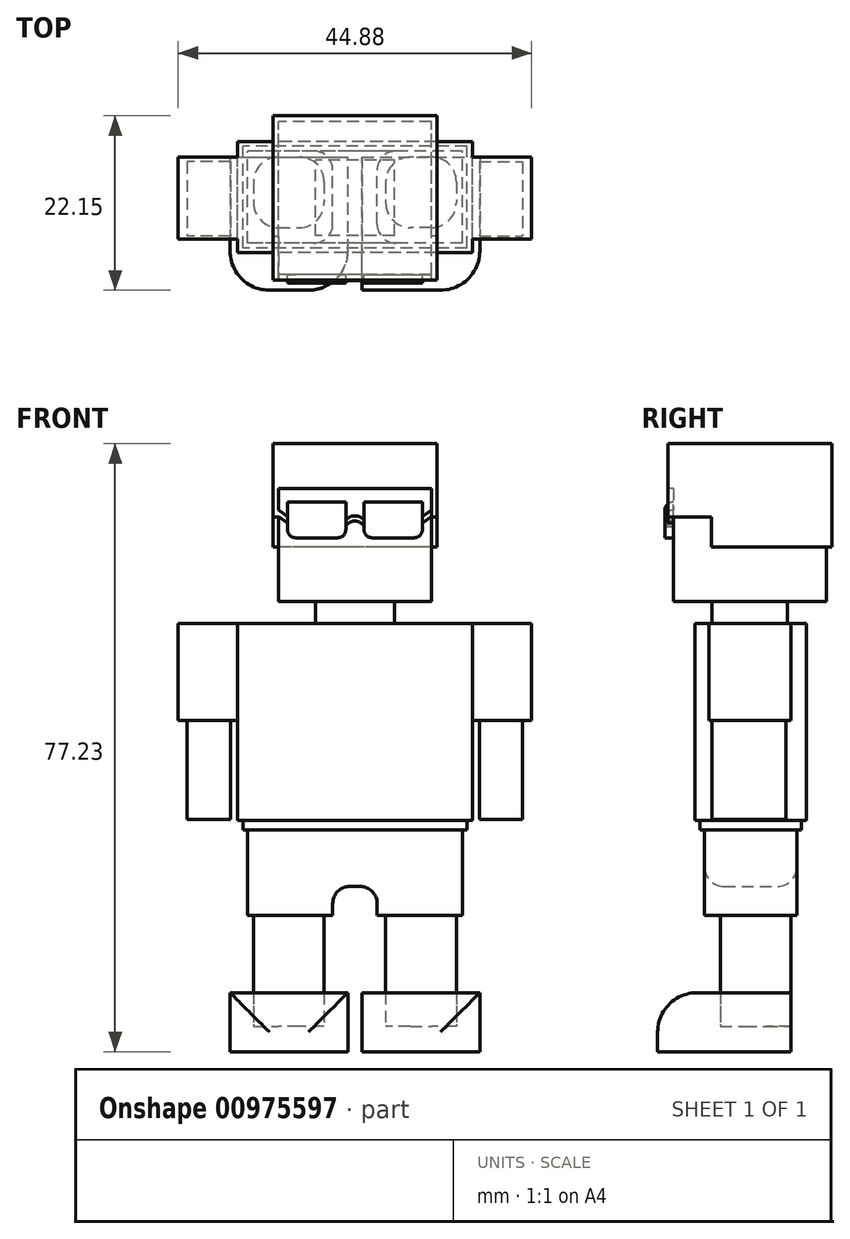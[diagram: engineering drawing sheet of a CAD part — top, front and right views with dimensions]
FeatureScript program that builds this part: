
annotation { "Feature Type Name" : "Feature", "Feature Type Description" : "" }
export const myFeature = defineFeature(function(context is Context, id is Id, definition is map)
    precondition{}
    {
        {
            var Q0;
            Q0=qCreatedBy(makeId("Top.planeOp"),FACE);
            var sketch = newSketch(context, id + "F0", { "sketchPlane" : qUnion([Q0])});
            skLineSegment(sketch, "E0.left", {"start": v(-15.87, 0) * mm, "end": v(-15.87, -16.94) * mm});
            skLineSegment(sketch, "E0.right", {"start": v(15.87, 0) * mm, "end": v(15.87, -16.94) * mm});
            skLineSegment(sketch, "E1", {"start": v(-15.87, 0) * mm, "end": v(15.87, 0) * mm});
            skLineSegment(sketch, "E2", {"start": v(-15.87, -16.94) * mm, "end": v(15.87, -16.94) * mm});
            skLineSegment(sketch, "E3.bottom", {"start": v(0.9, -16.94) * mm, "end": v(-0.9, -16.94) * mm});
            skLineSegment(sketch, "E3.top", {"start": v(0.9, 0) * mm, "end": v(-0.9, 0) * mm});
            skLineSegment(sketch, "E3.left", {"start": v(0.9, -16.94) * mm, "end": v(0.9, 0) * mm});
            skLineSegment(sketch, "E3.right", {"start": v(-0.9, -16.94) * mm, "end": v(-0.9, 0) * mm});
            skPoint(sketch, "E3.middle", {"position": v(0, -8.47) * mm});
            skPoint(sketch, "E3.middle.positionSnap0", {"position": v(15.87, -8.47) * mm});
            skPoint(sketch, "E3.centerSnap0", {"position": v(15.87, -8.47) * mm});
            skSolve(sketch);
        }
        {
            var Q0;
            {var subQ0=sQuery(id+"F0.wireOp",EDGE,"E0.left");Q0=makeQuery(id+"F0.imprint","IMPRINT",FACE,{"disambiguationData":[TD([[makeQuery(id+"F0.imprint","IMPRINT",EDGE,{"derivedFrom":subQ0}),1.0]])]});}
            var Q1;
            {var subQ0=sQuery(id+"F0.wireOp",EDGE,"E3.left");Q1=makeQuery(id+"F0.imprint","IMPRINT",FACE,{"disambiguationData":[TD([[makeQuery(id+"F0.imprint","IMPRINT",EDGE,{"derivedFrom":subQ0}),1.0]])]});}
            var Q2;
            {var subQ0=sQuery(id+"F0.wireOp",EDGE,"E0.right");Q2=makeQuery(id+"F0.imprint","IMPRINT",FACE,{"disambiguationData":[TD([[makeQuery(id+"F0.imprint","IMPRINT",EDGE,{"derivedFrom":subQ0}),-1.0]])]});}
            extrude(context, id + "F1", {"entities" : qUnion([Q0, Q1, Q2]), "depth" : 7.5 * mm, "offsetDistance" : 25 * mm});
        }
        {
            var Q0;
            {var subQ0=sQuery(id+"F0.wireOp",EDGE,"E3.left");Q0=makeQuery(id+"F0.imprint","IMPRINT",FACE,{"disambiguationData":[TD([[makeQuery(id+"F0.imprint","IMPRINT",EDGE,{"derivedFrom":subQ0}),1.0]])]});}
            extrude(context, id + "F2", {"entities" : qUnion([Q0]), "operationType" : NewBodyOperationType.REMOVE, "depth" : 14.2 * mm, "offsetDistance" : 25 * mm});
        }
        {
            var Q0;
            Q0=makeQuery(id+"F1.opExtrude","SWEPT_EDGE",EDGE,{"disambiguationData":[OSD([sQuery(id+"F0.wireOp",EDGE,"E0.left"),sQuery(id+"F0.wireOp",EDGE,"E2")])]});
            var Q1;
            Q1=makeQuery(id+"F2.boolean.opBoolean","COPY",EDGE,{"derivedFrom":makeQuery(id+"F2.opExtrude","SWEPT_EDGE",EDGE,{"disambiguationData":[OSD([sQuery(id+"F0.wireOp",EDGE,"E2"),sQuery(id+"F0.wireOp",EDGE,"E3.right")])]})});
            var Q2;
            Q2=makeQuery(id+"F2.boolean.opBoolean","COPY",EDGE,{"derivedFrom":makeQuery(id+"F2.opExtrude","SWEPT_EDGE",EDGE,{"disambiguationData":[OSD([sQuery(id+"F0.wireOp",EDGE,"E2"),sQuery(id+"F0.wireOp",EDGE,"E3.left")])]})});
            var Q3;
            Q3=makeQuery(id+"F1.opExtrude","SWEPT_EDGE",EDGE,{"disambiguationData":[OSD([sQuery(id+"F0.wireOp",EDGE,"E0.right"),sQuery(id+"F0.wireOp",EDGE,"E2")])]});
            var Q4;
            {var subQ0=sQuery(id+"F0.wireOp",EDGE,"E0.left");var subQ1=sQuery(id+"F0.wireOp",EDGE,"E2");Q4=makeQuery(id+"F2.boolean.opBoolean","SPLIT",EDGE,{"disambiguationData":[TD([makeQuery(id+"F1.opExtrude","SWEPT_FACE",FACE,{"disambiguationData":[OSD([subQ0])]})])],"derivedFrom":makeQuery(id+"F1.opExtrude","CAP_EDGE",EDGE,{"disambiguationData":[OSD([subQ1])],"isStart":false})});}
            var Q5;
            {var subQ0=sQuery(id+"F0.wireOp",EDGE,"E2");var subQ1=sQuery(id+"F0.wireOp",EDGE,"E0.right");Q5=makeQuery(id+"F2.boolean.opBoolean","SPLIT",EDGE,{"disambiguationData":[TD([makeQuery(id+"F1.opExtrude","SWEPT_FACE",FACE,{"disambiguationData":[OSD([subQ1])]})])],"derivedFrom":makeQuery(id+"F1.opExtrude","CAP_EDGE",EDGE,{"disambiguationData":[OSD([subQ0])],"isStart":false})});}
            fillet(context, id + "F3", {"entities" : qUnion([Q0, Q1, Q2, Q3, Q4, Q5]), "tangentPropagation" : true, "radius" : 5 * mm, "defaultsChanged" : false, "vertexSettings" : [], "allowEdgeOverflow" : false});
        }
        {
            var Q0;
            {var subQ0=sQuery(id+"F0.wireOp",EDGE,"E0.left");var subQ1=sQuery(id+"F0.wireOp",EDGE,"E2");var subQ2=sQuery(id+"F0.wireOp",EDGE,"E1");Q0=makeQuery(id+"F2.boolean.opBoolean","SPLIT",FACE,{"disambiguationData":[TD([makeQuery(id+"F1.opExtrude","SWEPT_FACE",FACE,{"disambiguationData":[OSD([subQ0])]})])],"derivedFrom":makeQuery(id+"F1.opExtrude","CAP_FACE",FACE,{"disambiguationData":[OSD([subQ0,sQuery(id+"F0.wireOp",EDGE,"E0.right"),subQ2,subQ1])],"isStart":false})});}
            var sketch = newSketch(context, id + "F4", { "sketchPlane" : qUnion([Q0])});
            skLineSegment(sketch, "E4.bottom", {"start": v(-3.9, -8.98) * mm, "end": v(-12.87, -8.98) * mm});
            skLineSegment(sketch, "E4.top", {"start": v(-3.9, -0.01) * mm, "end": v(-12.87, -0.01) * mm});
            skLineSegment(sketch, "E4.left", {"start": v(-3.9, -8.98) * mm, "end": v(-3.9, -0.01) * mm});
            skLineSegment(sketch, "E4.right", {"start": v(-12.87, -8.98) * mm, "end": v(-12.87, -0.01) * mm});
            skPoint(sketch, "E4.middle", {"position": v(-8.39, -4.5) * mm});
            skPoint(sketch, "E4.middle.positionSnap0", {"position": v(-8.39, 0) * mm});
            skPoint(sketch, "E4.centerSnap0", {"position": v(-8.39, 0) * mm});
            skLineSegment(sketch, "E5.MirrorCS", {"start": v(3.9, -8.98) * mm, "end": v(3.9, -0.01) * mm});
            skLineSegment(sketch, "E6.MirrorCS", {"start": v(3.9, -8.98) * mm, "end": v(12.87, -8.98) * mm});
            skLineSegment(sketch, "E7.MirrorCS", {"start": v(12.87, -8.98) * mm, "end": v(12.87, -0.01) * mm});
            skLineSegment(sketch, "E8.MirrorCS", {"start": v(3.9, -0.01) * mm, "end": v(12.87, -0.01) * mm});
            skSolve(sketch);
        }
        {
            var Q0;
            Q0=makeQuery(id+"F4.imprint","IMPRINT",FACE,{"disambiguationData":[TD([[makeQuery(id+"F4.imprint","IMPRINT",EDGE,{"derivedFrom":sQuery(id+"F4.wireOp",EDGE,"E4.bottom")}),-1.0]])]});
            var Q1;
            Q1=makeQuery(id+"F4.imprint","IMPRINT",FACE,{"disambiguationData":[TD([[makeQuery(id+"F4.imprint","IMPRINT",EDGE,{"derivedFrom":sQuery(id+"F4.wireOp",EDGE,"E5.MirrorCS")}),-1.0]])]});
            extrude(context, id + "F5", {"entities" : qUnion([Q0, Q1]), "depth" : 13.5 * mm, "offsetDistance" : 25 * mm, "hasSecondDirection" : true, "secondDirectionOppositeDirection" : true, "secondDirectionDepth" : 4.3 * mm});
        }
        {
            var Q0;
            Q0=makeQuery(id+"F5.opExtrude","SWEPT_EDGE",EDGE,{"disambiguationData":[OSD([sQuery(id+"F4.wireOp",EDGE,"E4.bottom"),sQuery(id+"F4.wireOp",EDGE,"E4.right")])]});
            var Q1;
            Q1=makeQuery(id+"F5.opExtrude","SWEPT_EDGE",EDGE,{"disambiguationData":[OSD([sQuery(id+"F4.wireOp",EDGE,"E4.bottom"),sQuery(id+"F4.wireOp",EDGE,"E4.left")])]});
            var Q2;
            Q2=makeQuery(id+"F5.opExtrude","SWEPT_EDGE",EDGE,{"disambiguationData":[OSD([sQuery(id+"F4.wireOp",EDGE,"E5.MirrorCS"),sQuery(id+"F4.wireOp",EDGE,"E6.MirrorCS")])]});
            var Q3;
            Q3=makeQuery(id+"F5.opExtrude","SWEPT_EDGE",EDGE,{"disambiguationData":[OSD([sQuery(id+"F4.wireOp",EDGE,"E4.top"),sQuery(id+"F4.wireOp",EDGE,"E4.right")])]});
            var Q4;
            Q4=makeQuery(id+"F5.opExtrude","SWEPT_EDGE",EDGE,{"disambiguationData":[OSD([sQuery(id+"F4.wireOp",EDGE,"E4.top"),sQuery(id+"F4.wireOp",EDGE,"E4.left")])]});
            var Q5;
            Q5=makeQuery(id+"F5.opExtrude","SWEPT_EDGE",EDGE,{"disambiguationData":[OSD([sQuery(id+"F4.wireOp",EDGE,"E6.MirrorCS"),sQuery(id+"F4.wireOp",EDGE,"E7.MirrorCS")])]});
            var Q6;
            Q6=makeQuery(id+"F5.opExtrude","SWEPT_EDGE",EDGE,{"disambiguationData":[OSD([sQuery(id+"F4.wireOp",EDGE,"E7.MirrorCS"),sQuery(id+"F4.wireOp",EDGE,"E8.MirrorCS")])]});
            var Q7;
            Q7=makeQuery(id+"F5.opExtrude","SWEPT_EDGE",EDGE,{"disambiguationData":[OSD([sQuery(id+"F4.wireOp",EDGE,"E5.MirrorCS"),sQuery(id+"F4.wireOp",EDGE,"E8.MirrorCS")])]});
            fillet(context, id + "F6", {"entities" : qUnion([Q0, Q1, Q2, Q3, Q4, Q5, Q6, Q7]), "tangentPropagation" : true, "radius" : 3.14 * mm, "defaultsChanged" : false, "vertexSettings" : [], "allowEdgeOverflow" : false});
        }
        {
            var Q0;
            Q0=makeQuery(id+"F5.opExtrude","CAP_FACE",FACE,{"disambiguationData":[OSD([sQuery(id+"F4.wireOp",EDGE,"E4.bottom"),sQuery(id+"F4.wireOp",EDGE,"E4.top"),sQuery(id+"F4.wireOp",EDGE,"E4.left"),sQuery(id+"F4.wireOp",EDGE,"E4.right")])],"isStart":false});
            var sketch = newSketch(context, id + "F7", { "sketchPlane" : qUnion([Q0])});
            skLineSegment(sketch, "E9.bottom", {"start": v(13.64, -10.96) * mm, "end": v(-13.64, -10.96) * mm});
            skLineSegment(sketch, "E9.top", {"start": v(13.64, 0.74) * mm, "end": v(-13.64, 0.74) * mm});
            skLineSegment(sketch, "E9.left", {"start": v(13.64, -10.96) * mm, "end": v(13.64, 0.74) * mm});
            skLineSegment(sketch, "E9.right", {"start": v(-13.64, -10.96) * mm, "end": v(-13.64, 0.74) * mm});
            skPoint(sketch, "E9.middle", {"position": v(0, -5.1) * mm});
            skSolve(sketch);
        }
        {
            var Q0;
            Q0 = qSketchRegion(id + "F7", true);
            extrude(context, id + "F8", {"entities" : qUnion([Q0]), "depth" : 7.2 * mm, "offsetDistance" : 25 * mm});
        }
        {
            var Q0;
            Q0=makeQuery(id+"F8.opExtrude","CAP_FACE",FACE,{"disambiguationData":[OSD([sQuery(id+"F7.wireOp",EDGE,"E9.bottom"),sQuery(id+"F7.wireOp",EDGE,"E9.top"),sQuery(id+"F7.wireOp",EDGE,"E9.left"),sQuery(id+"F7.wireOp",EDGE,"E9.right")])],"isStart":true});
            var sketch = newSketch(context, id + "F9", { "sketchPlane" : qUnion([Q0])});
            skLineSegment(sketch, "E10.bottom", {"start": v(-13.64, 10.96) * mm, "end": v(-2.82, 10.96) * mm});
            skLineSegment(sketch, "E10.top", {"start": v(-13.64, -0.74) * mm, "end": v(-2.82, -0.74) * mm});
            skLineSegment(sketch, "E10.left", {"start": v(-13.64, 10.96) * mm, "end": v(-13.64, -0.74) * mm});
            skLineSegment(sketch, "E10.right", {"start": v(-2.82, 10.96) * mm, "end": v(-2.82, -0.74) * mm});
            skLineSegment(sketch, "E11.MirrorCS", {"start": v(13.64, 10.96) * mm, "end": v(2.82, 10.96) * mm});
            skLineSegment(sketch, "E12.MirrorCS", {"start": v(13.64, 10.96) * mm, "end": v(13.64, -0.74) * mm});
            skLineSegment(sketch, "E13.MirrorCS", {"start": v(13.64, -0.74) * mm, "end": v(2.82, -0.74) * mm});
            skLineSegment(sketch, "E14.MirrorCS", {"start": v(2.82, 10.96) * mm, "end": v(2.82, -0.74) * mm});
            skSolve(sketch);
        }
        {
            var Q0;
            Q0=makeQuery(id+"F9.imprint","IMPRINT",FACE,{"disambiguationData":[TD([[makeQuery(id+"F9.imprint","IMPRINT",EDGE,{"derivedFrom":sQuery(id+"F9.wireOp",EDGE,"E10.bottom")}),1.0]])]});
            var Q1;
            Q1=makeQuery(id+"F9.imprint","IMPRINT",FACE,{"disambiguationData":[TD([[makeQuery(id+"F9.imprint","IMPRINT",EDGE,{"derivedFrom":sQuery(id+"F9.wireOp",EDGE,"E11.MirrorCS")}),1.0]])]});
            extrude(context, id + "F10", {"entities" : qUnion([Q0, Q1]), "operationType" : NewBodyOperationType.ADD, "depth" : 3.7 * mm, "offsetDistance" : 25 * mm, "hasSecondDirection" : true, "secondDirectionOppositeDirection" : true, "secondDirectionDepth" : 2.3 * mm});
        }
        {
            var Q0;
            Q0=makeQuery(id+"F10.boolean.opBoolean","INTERSECT",EDGE,{"derivedFrom":[makeQuery(id+"F8.opExtrude","CAP_FACE",FACE,{"disambiguationData":[OSD([sQuery(id+"F7.wireOp",EDGE,"E9.bottom"),sQuery(id+"F7.wireOp",EDGE,"E9.top"),sQuery(id+"F7.wireOp",EDGE,"E9.left"),sQuery(id+"F7.wireOp",EDGE,"E9.right")])],"isStart":true}),makeQuery(id+"F10.opExtrude","SWEPT_FACE",FACE,{"disambiguationData":[OSD([sQuery(id+"F9.wireOp",EDGE,"E14.MirrorCS")])]})]});
            var Q1;
            Q1=makeQuery(id+"F10.boolean.opBoolean","INTERSECT",EDGE,{"derivedFrom":[makeQuery(id+"F8.opExtrude","CAP_FACE",FACE,{"disambiguationData":[OSD([sQuery(id+"F7.wireOp",EDGE,"E9.bottom"),sQuery(id+"F7.wireOp",EDGE,"E9.top"),sQuery(id+"F7.wireOp",EDGE,"E9.left"),sQuery(id+"F7.wireOp",EDGE,"E9.right")])],"isStart":true}),makeQuery(id+"F10.opExtrude","SWEPT_FACE",FACE,{"disambiguationData":[OSD([sQuery(id+"F9.wireOp",EDGE,"E10.right")])]})]});
            fillet(context, id + "F11", {"entities" : qUnion([Q0, Q1]), "tangentPropagation" : true, "radius" : 2.17 * mm, "defaultsChanged" : false, "vertexSettings" : [], "allowEdgeOverflow" : false});
        }
        {
            var Q0;
            {var subQ0=sQuery(id+"F7.wireOp",EDGE,"E9.top");Q0=makeQuery(id+"F11.opFillet","BLEND_EDGE",EDGE,{"blendedFrom":[makeQuery(id+"F10.boolean.opBoolean","INTERSECT",EDGE,{"derivedFrom":[makeQuery(id+"F8.opExtrude","CAP_FACE",FACE,{"disambiguationData":[OSD([sQuery(id+"F7.wireOp",EDGE,"E9.bottom"),subQ0,sQuery(id+"F7.wireOp",EDGE,"E9.left"),sQuery(id+"F7.wireOp",EDGE,"E9.right")])],"isStart":true}),makeQuery(id+"F10.opExtrude","SWEPT_FACE",FACE,{"disambiguationData":[OSD([sQuery(id+"F9.wireOp",EDGE,"E14.MirrorCS")])]})]}),makeQuery(id+"F10.boolean.opBoolean","MERGE",FACE,{"derivedFrom":[makeQuery(id+"F8.opExtrude","SWEPT_FACE",FACE,{"disambiguationData":[OSD([subQ0])]}),makeQuery(id+"F10.opExtrude","SWEPT_FACE",FACE,{"disambiguationData":[OSD([sQuery(id+"F9.wireOp",EDGE,"E10.top")])]}),makeQuery(id+"F10.opExtrude","SWEPT_FACE",FACE,{"disambiguationData":[OSD([sQuery(id+"F9.wireOp",EDGE,"E13.MirrorCS")])]})]})],"blendedInto":[makeQuery(id+"F10.boolean.opBoolean","MERGE",FACE,{"derivedFrom":[makeQuery(id+"F8.opExtrude","SWEPT_FACE",FACE,{"disambiguationData":[OSD([subQ0])]}),makeQuery(id+"F10.opExtrude","SWEPT_FACE",FACE,{"disambiguationData":[OSD([sQuery(id+"F9.wireOp",EDGE,"E10.top")])]}),makeQuery(id+"F10.opExtrude","SWEPT_FACE",FACE,{"disambiguationData":[OSD([sQuery(id+"F9.wireOp",EDGE,"E13.MirrorCS")])]})]})]});}
            var Q1;
            {var subQ0=sQuery(id+"F7.wireOp",EDGE,"E9.bottom");Q1=makeQuery(id+"F11.opFillet","BLEND_EDGE",EDGE,{"blendedFrom":[makeQuery(id+"F10.boolean.opBoolean","INTERSECT",EDGE,{"derivedFrom":[makeQuery(id+"F8.opExtrude","CAP_FACE",FACE,{"disambiguationData":[OSD([subQ0,sQuery(id+"F7.wireOp",EDGE,"E9.top"),sQuery(id+"F7.wireOp",EDGE,"E9.left"),sQuery(id+"F7.wireOp",EDGE,"E9.right")])],"isStart":true}),makeQuery(id+"F10.opExtrude","SWEPT_FACE",FACE,{"disambiguationData":[OSD([sQuery(id+"F9.wireOp",EDGE,"E10.right")])]})]}),makeQuery(id+"F10.boolean.opBoolean","MERGE",FACE,{"derivedFrom":[makeQuery(id+"F8.opExtrude","SWEPT_FACE",FACE,{"disambiguationData":[OSD([subQ0])]}),makeQuery(id+"F10.opExtrude","SWEPT_FACE",FACE,{"disambiguationData":[OSD([sQuery(id+"F9.wireOp",EDGE,"E10.bottom")])]}),makeQuery(id+"F10.opExtrude","SWEPT_FACE",FACE,{"disambiguationData":[OSD([sQuery(id+"F9.wireOp",EDGE,"E11.MirrorCS")])]})]})],"blendedInto":[makeQuery(id+"F10.boolean.opBoolean","MERGE",FACE,{"derivedFrom":[makeQuery(id+"F8.opExtrude","SWEPT_FACE",FACE,{"disambiguationData":[OSD([subQ0])]}),makeQuery(id+"F10.opExtrude","SWEPT_FACE",FACE,{"disambiguationData":[OSD([sQuery(id+"F9.wireOp",EDGE,"E10.bottom")])]}),makeQuery(id+"F10.opExtrude","SWEPT_FACE",FACE,{"disambiguationData":[OSD([sQuery(id+"F9.wireOp",EDGE,"E11.MirrorCS")])]})]})]});}
            fillet(context, id + "F12", {"entities" : qUnion([Q0, Q1]), "tangentPropagation" : true, "radius" : 2.41 * mm, "defaultsChanged" : false, "vertexSettings" : [], "allowEdgeOverflow" : false});
        }
        {
            var Q0;
            Q0=makeQuery(id+"F8.opExtrude","CAP_FACE",FACE,{"disambiguationData":[OSD([sQuery(id+"F7.wireOp",EDGE,"E9.bottom"),sQuery(id+"F7.wireOp",EDGE,"E9.top"),sQuery(id+"F7.wireOp",EDGE,"E9.left"),sQuery(id+"F7.wireOp",EDGE,"E9.right")])],"isStart":false});
            var sketch = newSketch(context, id + "F13", { "sketchPlane" : qUnion([Q0])});
            skLineSegment(sketch, "E15.bottom", {"start": v(14.22, -11.56) * mm, "end": v(-14.22, -11.56) * mm});
            skLineSegment(sketch, "E15.top", {"start": v(14.22, 1.34) * mm, "end": v(-14.22, 1.34) * mm});
            skLineSegment(sketch, "E15.left", {"start": v(14.22, -11.56) * mm, "end": v(14.22, 1.34) * mm});
            skLineSegment(sketch, "E15.right", {"start": v(-14.22, -11.56) * mm, "end": v(-14.22, 1.34) * mm});
            skPoint(sketch, "E15.middle", {"position": v(0, -5.1) * mm});
            skPoint(sketch, "E15.middle.positionSnap0", {"position": v(13.64, -5.1) * mm});
            skPoint(sketch, "E15.centerSnap0", {"position": v(13.64, -5.1) * mm});
            skSolve(sketch);
        }
        {
            var Q0;
            Q0 = qSketchRegion(id + "F13", true);
            extrude(context, id + "F14", {"entities" : qUnion([Q0]), "operationType" : NewBodyOperationType.ADD, "depth" : 1.2 * mm, "offsetDistance" : 25 * mm});
        }
        {
            var Q0;
            Q0=makeQuery(id+"F14.opExtrude","CAP_FACE",FACE,{"disambiguationData":[OSD([sQuery(id+"F13.wireOp",EDGE,"E15.bottom"),sQuery(id+"F13.wireOp",EDGE,"E15.top"),sQuery(id+"F13.wireOp",EDGE,"E15.left"),sQuery(id+"F13.wireOp",EDGE,"E15.right")])],"isStart":false});
            var sketch = newSketch(context, id + "F15", { "sketchPlane" : qUnion([Q0])});
            skLineSegment(sketch, "E16.bottom", {"start": v(14.94, -12.17) * mm, "end": v(-14.94, -12.17) * mm});
            skLineSegment(sketch, "E16.top", {"start": v(14.94, 1.95) * mm, "end": v(-14.94, 1.95) * mm});
            skLineSegment(sketch, "E16.left", {"start": v(14.94, -12.17) * mm, "end": v(14.94, 1.95) * mm});
            skLineSegment(sketch, "E16.right", {"start": v(-14.94, -12.17) * mm, "end": v(-14.94, 1.95) * mm});
            skPoint(sketch, "E16.middle", {"position": v(0, -5.1) * mm});
            skPoint(sketch, "E16.middle.positionSnap0", {"position": v(14.22, -5.1) * mm});
            skPoint(sketch, "E16.centerSnap0", {"position": v(14.22, -5.1) * mm});
            skSolve(sketch);
        }
        {
            var Q0;
            Q0=makeQuery(id+"F15.imprint","IMPRINT",FACE,{"disambiguationData":[TD([[makeQuery(id+"F15.imprint","IMPRINT",EDGE,{"derivedFrom":sQuery(id+"F15.wireOp",EDGE,"E16.bottom")}),-1.0]])]});
            var Q1;
            Q1=makeQuery(id+"F15.imprint","IMPRINT",FACE,{"disambiguationData":[TD([[makeQuery(id+"F15.imprint","IMPRINT",EDGE,{"derivedFrom":makeQuery(id+"F14.opExtrude","CAP_EDGE",EDGE,{"disambiguationData":[OSD([sQuery(id+"F13.wireOp",EDGE,"E15.bottom")])],"isStart":false})}),-1.0]])]});
            extrude(context, id + "F16", {"entities" : qUnion([Q0, Q1]), "depth" : 25 * mm, "offsetDistance" : 25 * mm});
        }
        {
            var Q0;
            Q0=makeQuery(id+"F16.opExtrude","SWEPT_FACE",FACE,{"disambiguationData":[OSD([sQuery(id+"F15.wireOp",EDGE,"E16.right")])]});
            var sketch = newSketch(context, id + "F17", { "sketchPlane" : qUnion([Q0])});
            skLineSegment(sketch, "E17.bottom", {"start": v(0, 54.4) * mm, "end": v(10.42, 54.4) * mm});
            skLineSegment(sketch, "E17.top", {"start": v(0, 42.1) * mm, "end": v(10.42, 42.1) * mm});
            skLineSegment(sketch, "E17.left", {"start": v(0, 54.4) * mm, "end": v(0, 42.1) * mm});
            skLineSegment(sketch, "E17.right", {"start": v(10.42, 54.4) * mm, "end": v(10.42, 42.1) * mm});
            skSolve(sketch);
        }
        {
            var Q0;
            Q0 = qSketchRegion(id + "F17", true);
            extrude(context, id + "F18", {"entities" : qUnion([Q0]), "operationType" : NewBodyOperationType.ADD, "depth" : 7.5 * mm, "offsetDistance" : 25 * mm, "hasSecondDirection" : true, "secondDirectionOppositeDirection" : true, "secondDirectionDepth" : 37.38 * mm});
        }
        {
            var Q0;
            {var subQ2=sQuery(id+"F17.wireOp",EDGE,"E17.top");Q0=makeQuery(id+"F18.boolean.opBoolean","SPLIT",FACE,{"disambiguationData":[TD([makeQuery(id+"F16.opExtrude","SWEPT_FACE",FACE,{"disambiguationData":[OSD([sQuery(id+"F15.wireOp",EDGE,"E16.right")])]})])],"derivedFrom":makeQuery(id+"F18.opExtrude","SWEPT_FACE",FACE,{"disambiguationData":[OSD([subQ2])]})});}
            var sketch = newSketch(context, id + "F19", { "sketchPlane" : qUnion([Q0])});
            skLineSegment(sketch, "E18.bottom", {"start": v(-15.8, 0.63) * mm, "end": v(-21.3, 0.63) * mm});
            skLineSegment(sketch, "E18.top", {"start": v(-15.8, 10.06) * mm, "end": v(-21.3, 10.06) * mm});
            skLineSegment(sketch, "E18.left", {"start": v(-15.8, 0.63) * mm, "end": v(-15.8, 10.06) * mm});
            skLineSegment(sketch, "E18.right", {"start": v(-21.3, 0.63) * mm, "end": v(-21.3, 10.06) * mm});
            skPoint(sketch, "E18.middle", {"position": v(-19.05, 5.34) * mm});
            skLineSegment(sketch, "E19.MirrorCS", {"start": v(15.8, 0.63) * mm, "end": v(21.3, 0.63) * mm});
            skLineSegment(sketch, "E20.MirrorCS", {"start": v(15.8, 0.63) * mm, "end": v(15.8, 10.06) * mm});
            skLineSegment(sketch, "E21.MirrorCS", {"start": v(15.8, 10.06) * mm, "end": v(21.3, 10.06) * mm});
            skLineSegment(sketch, "E22.MirrorCS", {"start": v(21.3, 0.63) * mm, "end": v(21.3, 10.06) * mm});
            skSolve(sketch);
        }
        {
            var Q0;
            Q0=makeQuery(id+"F19.imprint","IMPRINT",FACE,{"disambiguationData":[TD([[makeQuery(id+"F19.imprint","IMPRINT",EDGE,{"derivedFrom":sQuery(id+"F19.wireOp",EDGE,"E18.bottom")}),-1.0]])]});
            var Q1;
            Q1=makeQuery(id+"F19.imprint","IMPRINT",FACE,{"disambiguationData":[TD([[makeQuery(id+"F19.imprint","IMPRINT",EDGE,{"derivedFrom":sQuery(id+"F19.wireOp",EDGE,"E19.MirrorCS")}),1.0]])]});
            extrude(context, id + "F20", {"entities" : qUnion([Q0, Q1]), "depth" : 12.6 * mm, "offsetDistance" : 25 * mm});
        }
        {
            var Q0;
            Q0=makeQuery(id+"F18.boolean.opBoolean","MERGE",FACE,{"derivedFrom":[makeQuery(id+"F16.opExtrude","CAP_FACE",FACE,{"disambiguationData":[OSD([sQuery(id+"F15.wireOp",EDGE,"E16.bottom"),sQuery(id+"F15.wireOp",EDGE,"E16.top"),sQuery(id+"F15.wireOp",EDGE,"E16.left"),sQuery(id+"F15.wireOp",EDGE,"E16.right")])],"isStart":false}),makeQuery(id+"F18.opExtrude","SWEPT_FACE",FACE,{"disambiguationData":[OSD([sQuery(id+"F17.wireOp",EDGE,"E17.bottom")])]})]});
            var sketch = newSketch(context, id + "F21", { "sketchPlane" : qUnion([Q0])});
            skLineSegment(sketch, "E23.bottom", {"start": v(5.03, -10) * mm, "end": v(-5.03, -10) * mm});
            skLineSegment(sketch, "E23.top", {"start": v(5.03, -0.42) * mm, "end": v(-5.03, -0.42) * mm});
            skLineSegment(sketch, "E23.left", {"start": v(5.03, -10) * mm, "end": v(5.03, -0.42) * mm});
            skLineSegment(sketch, "E23.right", {"start": v(-5.03, -10) * mm, "end": v(-5.03, -0.42) * mm});
            skPoint(sketch, "E23.middle", {"position": v(0, -5.21) * mm});
            skPoint(sketch, "E23.middle.positionSnap0", {"position": v(22.44, -5.21) * mm});
            skPoint(sketch, "E23.centerSnap0", {"position": v(22.44, -5.21) * mm});
            skSolve(sketch);
        }
        {
            var Q0;
            Q0 = qSketchRegion(id + "F21", true);
            extrude(context, id + "F22", {"entities" : qUnion([Q0]), "depth" : 2.8 * mm, "offsetDistance" : 25 * mm});
        }
        {
            var Q0;
            Q0=makeQuery(id+"F22.opExtrude","CAP_FACE",FACE,{"disambiguationData":[OSD([sQuery(id+"F21.wireOp",EDGE,"E23.bottom"),sQuery(id+"F21.wireOp",EDGE,"E23.top"),sQuery(id+"F21.wireOp",EDGE,"E23.left"),sQuery(id+"F21.wireOp",EDGE,"E23.right")])],"isStart":false});
            var sketch = newSketch(context, id + "F23", { "sketchPlane" : qUnion([Q0])});
            skLineSegment(sketch, "E24.bottom", {"start": v(9.72, -14.93) * mm, "end": v(-9.72, -14.93) * mm});
            skLineSegment(sketch, "E24.top", {"start": v(9.72, 4.5) * mm, "end": v(-9.72, 4.5) * mm});
            skLineSegment(sketch, "E24.left", {"start": v(9.72, -14.93) * mm, "end": v(9.72, 4.5) * mm});
            skLineSegment(sketch, "E24.right", {"start": v(-9.72, -14.93) * mm, "end": v(-9.72, 4.5) * mm});
            skPoint(sketch, "E24.middle", {"position": v(0, -5.21) * mm});
            skPoint(sketch, "E24.middle.positionSnap0", {"position": v(5.03, -5.21) * mm});
            skPoint(sketch, "E24.centerSnap0", {"position": v(5.03, -5.21) * mm});
            skSolve(sketch);
        }
        {
            var Q0;
            Q0=makeQuery(id+"F23.imprint","IMPRINT",FACE,{"disambiguationData":[TD([[makeQuery(id+"F23.imprint","IMPRINT",EDGE,{"derivedFrom":sQuery(id+"F23.wireOp",EDGE,"E24.bottom")}),-1.0]])]});
            var Q1;
            Q1=makeQuery(id+"F23.imprint","IMPRINT",FACE,{"disambiguationData":[TD([[makeQuery(id+"F23.imprint","IMPRINT",EDGE,{"derivedFrom":makeQuery(id+"F22.opExtrude","CAP_EDGE",EDGE,{"disambiguationData":[OSD([sQuery(id+"F21.wireOp",EDGE,"E23.bottom")])],"isStart":false})}),-1.0]])]});
            extrude(context, id + "F24", {"entities" : qUnion([Q0, Q1]), "operationType" : NewBodyOperationType.ADD, "depth" : 19.43 * mm, "offsetDistance" : 25 * mm});
        }
        {
            var Q0;
            Q0=makeQuery(id+"F24.opExtrude","CAP_FACE",FACE,{"disambiguationData":[OSD([sQuery(id+"F23.wireOp",EDGE,"E24.bottom"),sQuery(id+"F23.wireOp",EDGE,"E24.top"),sQuery(id+"F23.wireOp",EDGE,"E24.left"),sQuery(id+"F23.wireOp",EDGE,"E24.right")])],"isStart":false});
            var sketch = newSketch(context, id + "F25", { "sketchPlane" : qUnion([Q0])});
            skLineSegment(sketch, "E25.bottom", {"start": v(10.44, -15.64) * mm, "end": v(-10.44, -15.64) * mm});
            skLineSegment(sketch, "E25.top", {"start": v(10.44, 5.21) * mm, "end": v(-10.44, 5.21) * mm});
            skLineSegment(sketch, "E25.left", {"start": v(10.44, -15.64) * mm, "end": v(10.44, 5.21) * mm});
            skLineSegment(sketch, "E25.right", {"start": v(-10.44, -15.64) * mm, "end": v(-10.44, 5.21) * mm});
            skPoint(sketch, "E25.middle", {"position": v(0, -5.21) * mm});
            skPoint(sketch, "E25.middle.positionSnap0", {"position": v(9.72, -5.21) * mm});
            skPoint(sketch, "E25.centerSnap0", {"position": v(9.72, -5.21) * mm});
            skLineSegment(sketch, "E26", {"start": v(-9.72, -14.93) * mm, "end": v(-9.72, -15.64) * mm});
            skLineSegment(sketch, "E27", {"start": v(9.72, -14.93) * mm, "end": v(9.72, -15.64) * mm});
            skLineSegment(sketch, "E28", {"start": v(-10.44, -10.08) * mm, "end": v(-9.72, -10.08) * mm});
            skLineSegment(sketch, "E29.MirrorCS", {"start": v(10.44, -10.08) * mm, "end": v(9.72, -10.08) * mm});
            skSolve(sketch);
        }
        {
            var Q0;
            {var subQ1=sQuery(id+"F25.wireOp",EDGE,"E25.top");Q0=makeQuery(id+"F25.imprint","IMPRINT",FACE,{"disambiguationData":[TD([[makeQuery(id+"F25.imprint","IMPRINT",EDGE,{"derivedFrom":subQ1}),1.0]])]});}
            extrude(context, id + "F26", {"entities" : qUnion([Q0]), "oppositeDirection" : true, "depth" : 12.5 * mm, "offsetDistance" : 25 * mm});
        }
        {
            var Q0;
            {var subQ1=sQuery(id+"F25.wireOp",EDGE,"E26");Q0=makeQuery(id+"F25.imprint","IMPRINT",FACE,{"disambiguationData":[TD([[makeQuery(id+"F25.imprint","IMPRINT",EDGE,{"derivedFrom":subQ1}),-1.0]])]});}
            var Q1;
            {var subQ4=sQuery(id+"F25.wireOp",EDGE,"E27");Q1=makeQuery(id+"F25.imprint","IMPRINT",FACE,{"disambiguationData":[TD([[makeQuery(id+"F25.imprint","IMPRINT",EDGE,{"derivedFrom":subQ4}),1.0]])]});}
            extrude(context, id + "F27", {"entities" : qUnion([Q0, Q1]), "operationType" : NewBodyOperationType.ADD, "oppositeDirection" : true, "depth" : 8.7 * mm, "offsetDistance" : 25 * mm});
        }
        {
            var Q0;
            {var subQ0=sQuery(id+"F25.wireOp",EDGE,"E26");Q0=makeQuery(id+"F25.imprint","IMPRINT",FACE,{"disambiguationData":[TD([[makeQuery(id+"F25.imprint","IMPRINT",EDGE,{"derivedFrom":subQ0}),1.0]])]});}
            extrude(context, id + "F28", {"entities" : qUnion([Q0]), "operationType" : NewBodyOperationType.ADD, "oppositeDirection" : true, "depth" : 5.1 * mm, "offsetDistance" : 25 * mm});
        }
        {
            var Q0;
            {var subQ1=sQuery(id+"F25.wireOp",EDGE,"E25.top");Q0=makeQuery(id+"F25.imprint","IMPRINT",FACE,{"disambiguationData":[TD([[makeQuery(id+"F25.imprint","IMPRINT",EDGE,{"derivedFrom":subQ1}),1.0]])]});}
            var Q1;
            {var subQ1=sQuery(id+"F25.wireOp",EDGE,"E26");Q1=makeQuery(id+"F25.imprint","IMPRINT",FACE,{"disambiguationData":[TD([[makeQuery(id+"F25.imprint","IMPRINT",EDGE,{"derivedFrom":subQ1}),-1.0]])]});}
            var Q2;
            {var subQ0=sQuery(id+"F25.wireOp",EDGE,"E26");Q2=makeQuery(id+"F25.imprint","IMPRINT",FACE,{"disambiguationData":[TD([[makeQuery(id+"F25.imprint","IMPRINT",EDGE,{"derivedFrom":subQ0}),1.0]])]});}
            var Q3;
            {var subQ3=makeQuery(id+"F24.opExtrude","CAP_EDGE",EDGE,{"disambiguationData":[OSD([sQuery(id+"F23.wireOp",EDGE,"E24.bottom")])],"isStart":false});Q3=makeQuery(id+"F25.imprint","IMPRINT",FACE,{"disambiguationData":[TD([[makeQuery(id+"F25.imprint","IMPRINT",EDGE,{"derivedFrom":subQ3}),-1.0]])]});}
            var Q4;
            {var subQ4=sQuery(id+"F25.wireOp",EDGE,"E27");Q4=makeQuery(id+"F25.imprint","IMPRINT",FACE,{"disambiguationData":[TD([[makeQuery(id+"F25.imprint","IMPRINT",EDGE,{"derivedFrom":subQ4}),1.0]])]});}
            extrude(context, id + "F29", {"entities" : qUnion([Q0, Q1, Q2, Q3, Q4]), "operationType" : NewBodyOperationType.ADD, "depth" : 0.6 * mm, "offsetDistance" : 25 * mm});
        }
        {
            var Q0;
            Q0=makeQuery(id+"F24.opExtrude","SWEPT_FACE",FACE,{"disambiguationData":[OSD([sQuery(id+"F23.wireOp",EDGE,"E24.bottom")])]});
            var sketch = newSketch(context, id + "F30", { "sketchPlane" : qUnion([Q0])});
            skLineSegment(sketch, "E30.bottom", {"start": v(-1.16, 65.28) * mm, "end": v(-8.56, 65.28) * mm});
            skLineSegment(sketch, "E30.top", {"start": v(-1.16, 69.8) * mm, "end": v(-8.56, 69.8) * mm});
            skLineSegment(sketch, "E30.left", {"start": v(-1.16, 65.28) * mm, "end": v(-1.16, 69.8) * mm});
            skLineSegment(sketch, "E30.right", {"start": v(-8.56, 65.28) * mm, "end": v(-8.56, 69.8) * mm});
            skPoint(sketch, "E30.middle", {"position": v(-5.51, 67.54) * mm});
            skPoint(sketch, "E31.MirrorP", {"position": v(5.51, 67.54) * mm});
            skLineSegment(sketch, "E32.MirrorCS", {"start": v(1.16, 69.8) * mm, "end": v(8.56, 69.8) * mm});
            skLineSegment(sketch, "E33.MirrorCS", {"start": v(1.16, 65.28) * mm, "end": v(8.56, 65.28) * mm});
            skLineSegment(sketch, "E34.MirrorCS", {"start": v(8.56, 65.28) * mm, "end": v(8.56, 69.8) * mm});
            skLineSegment(sketch, "E35.MirrorCS", {"start": v(1.16, 65.28) * mm, "end": v(1.16, 69.8) * mm});
            skArc(sketch, "E36", {"start": v(1.16, 66.72) * mm, "mid": v(0, 67.4) * mm, "end": v(-1.16, 66.75) * mm});
            skArc(sketch, "E37", {"start": v(1.16, 67.54) * mm, "mid": v(0, 68.07) * mm, "end": v(-1.16, 67.54) * mm});
            skLineSegment(sketch, "E38", {"start": v(-8.56, 67.98) * mm, "end": v(-9.72, 68.8) * mm});
            skLineSegment(sketch, "E39", {"start": v(-9.72, 68.8) * mm, "end": v(-9.72, 67.98) * mm});
            skLineSegment(sketch, "E40", {"start": v(-9.72, 67.98) * mm, "end": v(-8.56, 67.16) * mm});
            skLineSegment(sketch, "E41.MirrorCS", {"start": v(8.56, 67.98) * mm, "end": v(9.72, 68.8) * mm});
            skLineSegment(sketch, "E42.MirrorCS", {"start": v(9.72, 67.98) * mm, "end": v(8.56, 67.16) * mm});
            skLineSegment(sketch, "E43.MirrorCS", {"start": v(9.72, 68.8) * mm, "end": v(9.72, 67.98) * mm});
            skSolve(sketch);
        }
        {
            var Q0;
            {var subQ0=sQuery(id+"F30.wireOp",EDGE,"E36");Q0=makeQuery(id+"F30.imprint","IMPRINT",FACE,{"disambiguationData":[TD([[makeQuery(id+"F30.imprint","IMPRINT",EDGE,{"derivedFrom":subQ0}),-1.0]])]});}
            extrude(context, id + "F31", {"entities" : qUnion([Q0]), "depth" : 0.8 * mm, "offsetDistance" : 25 * mm});
        }
        {
            var Q0;
            {var subQ4=sQuery(id+"F30.wireOp",EDGE,"E32.MirrorCS");Q0=makeQuery(id+"F30.imprint","IMPRINT",FACE,{"disambiguationData":[TD([[makeQuery(id+"F30.imprint","IMPRINT",EDGE,{"derivedFrom":subQ4}),-1.0]])]});}
            var Q1;
            {var subQ3=sQuery(id+"F30.wireOp",EDGE,"E30.bottom");Q1=makeQuery(id+"F30.imprint","IMPRINT",FACE,{"disambiguationData":[TD([[makeQuery(id+"F30.imprint","IMPRINT",EDGE,{"derivedFrom":subQ3}),-1.0]])]});}
            extrude(context, id + "F32", {"entities" : qUnion([Q0, Q1]), "operationType" : NewBodyOperationType.ADD, "depth" : 1.1 * mm, "offsetDistance" : 25 * mm});
        }
        {
            var Q0;
            {var subQ0=sQuery(id+"F30.wireOp",EDGE,"E38");Q0=makeQuery(id+"F30.imprint","IMPRINT",FACE,{"disambiguationData":[TD([[makeQuery(id+"F30.imprint","IMPRINT",EDGE,{"derivedFrom":subQ0}),1.0]])]});}
            var Q1;
            {var subQ0=sQuery(id+"F30.wireOp",EDGE,"E41.MirrorCS");Q1=makeQuery(id+"F30.imprint","IMPRINT",FACE,{"disambiguationData":[TD([[makeQuery(id+"F30.imprint","IMPRINT",EDGE,{"derivedFrom":subQ0}),-1.0]])]});}
            extrude(context, id + "F33", {"entities" : qUnion([Q0, Q1]), "operationType" : NewBodyOperationType.ADD, "depth" : 0.7 * mm, "offsetDistance" : 25 * mm});
        }
        {
            var Q0;
            Q0=makeQuery(id+"F32.opExtrude","SWEPT_EDGE",EDGE,{"disambiguationData":[OSD([sQuery(id+"F30.wireOp",EDGE,"E30.bottom"),sQuery(id+"F30.wireOp",EDGE,"E30.left")])]});
            var Q1;
            Q1=makeQuery(id+"F32.opExtrude","SWEPT_EDGE",EDGE,{"disambiguationData":[OSD([sQuery(id+"F30.wireOp",EDGE,"E30.bottom"),sQuery(id+"F30.wireOp",EDGE,"E30.right")])]});
            var Q2;
            Q2=makeQuery(id+"F32.opExtrude","SWEPT_EDGE",EDGE,{"disambiguationData":[OSD([sQuery(id+"F30.wireOp",EDGE,"E33.MirrorCS"),sQuery(id+"F30.wireOp",EDGE,"E35.MirrorCS")])]});
            var Q3;
            Q3=makeQuery(id+"F32.opExtrude","SWEPT_EDGE",EDGE,{"disambiguationData":[OSD([sQuery(id+"F30.wireOp",EDGE,"E33.MirrorCS"),sQuery(id+"F30.wireOp",EDGE,"E34.MirrorCS")])]});
            var Q4;
            Q4=makeQuery(id+"F32.opExtrude","CAP_EDGE",EDGE,{"disambiguationData":[OSD([sQuery(id+"F30.wireOp",EDGE,"E30.top")])],"isStart":false});
            var Q5;
            Q5=makeQuery(id+"F32.opExtrude","CAP_EDGE",EDGE,{"disambiguationData":[OSD([sQuery(id+"F30.wireOp",EDGE,"E32.MirrorCS")])],"isStart":false});
            fillet(context, id + "F34", {"entities" : qUnion([Q0, Q1, Q2, Q3, Q4, Q5]), "tangentPropagation" : true, "radius" : 1.04 * mm, "defaultsChanged" : false, "vertexSettings" : [], "allowEdgeOverflow" : false});
        }
    });
